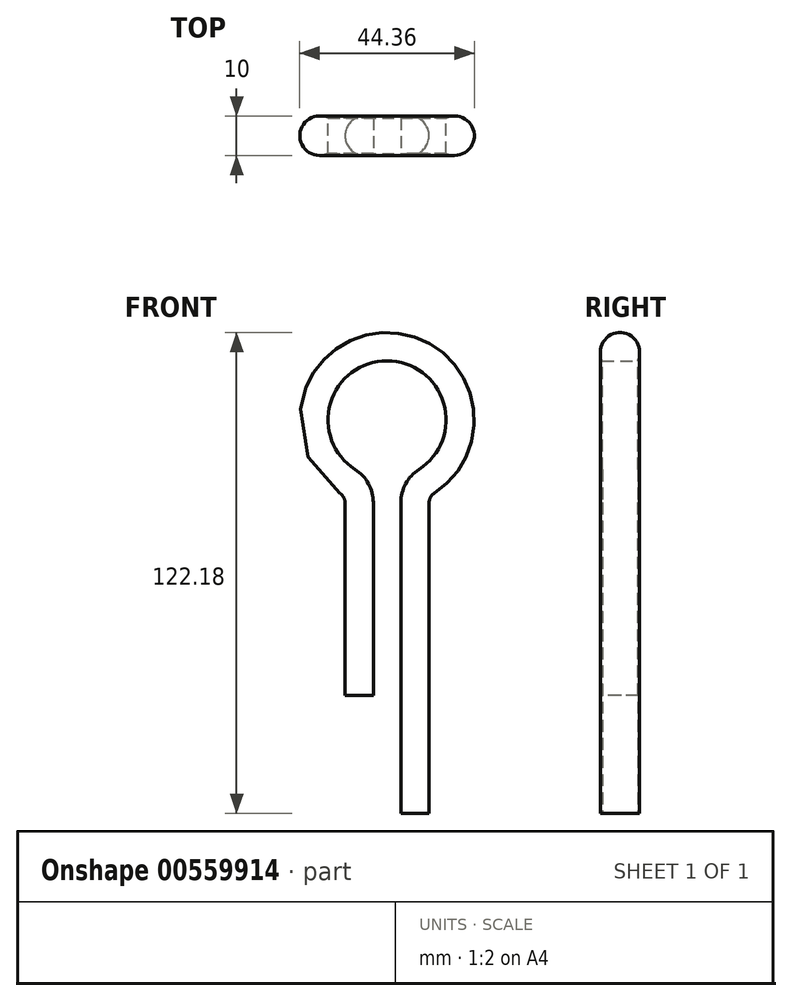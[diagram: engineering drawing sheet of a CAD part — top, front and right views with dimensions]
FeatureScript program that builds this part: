
annotation { "Feature Type Name" : "Feature", "Feature Type Description" : "" }
export const myFeature = defineFeature(function(context is Context, id is Id, definition is map)
    precondition{}
    {
        {
            var Q0;
            Q0=qCreatedBy(makeId("Front.planeOp"),FACE);
            var sketch = newSketch(context, id + "F0", { "sketchPlane" : qUnion([Q0])});
            skArc(sketch, "E0", {"start": v(11.6, 57.38) * mm, "mid": v(3.5, 85) * mm, "end": v(-4.6, 57.38) * mm});
            skLineSegment(sketch, "E1", {"start": v(0, 48.96) * mm, "end": v(0, 0) * mm});
            skLineSegment(sketch, "E2", {"start": v(7, 48.96) * mm, "end": v(7, -30) * mm});
            skArc(sketch, "E3.filletArc", {"start": v(0, 48.96) * mm, "mid": v(-1.23, 53.75) * mm, "end": v(-4.6, 57.38) * mm});
            skArc(sketch, "E4.filletArc", {"start": v(11.6, 57.38) * mm, "mid": v(8.23, 53.75) * mm, "end": v(7, 48.96) * mm});
            skSolve(sketch);
        }
        {
            var Q0;
            Q0=qCreatedBy(makeId("Top.planeOp"),FACE);
            var sketch = newSketch(context, id + "F1", { "sketchPlane" : qUnion([Q0])});
            skArc(sketch, "E5", {"start": v(0, 4.5) * mm, "mid": v(-7.18, 0) * mm, "end": v(0, -4.5) * mm});
            skLineSegment(sketch, "E6", {"start": v(0, 4.5) * mm, "end": v(0, -4.5) * mm});
            skSolve(sketch);
        }
        {
            var Q0;
            Q0=makeQuery(id+"F1.imprint","IMPRINT",FACE,{"disambiguationData":[TD([[makeQuery(id+"F1.imprint","IMPRINT",EDGE,{"derivedFrom":sQuery(id+"F1.wireOp",EDGE,"E5")}),1.0]])]});
            var Q1;
            Q1=sQuery(id+"F0.wireOp",EDGE,"E1");
            var Q2;
            Q2=sQuery(id+"F0.wireOp",EDGE,"E0");
            var Q3;
            Q3=sQuery(id+"F0.wireOp",EDGE,"E2");
            var Q4;
            Q4=sQuery(id+"F0.wireOp",EDGE,"E3.filletArc");
            var Q5;
            Q5=sQuery(id+"F0.wireOp",EDGE,"E4.filletArc");
            sweep(context, id + "F2", {"profiles" : qUnion([Q0]), "path" : qUnion([Q1, Q2, Q3, Q4, Q5])});
        }
    });
